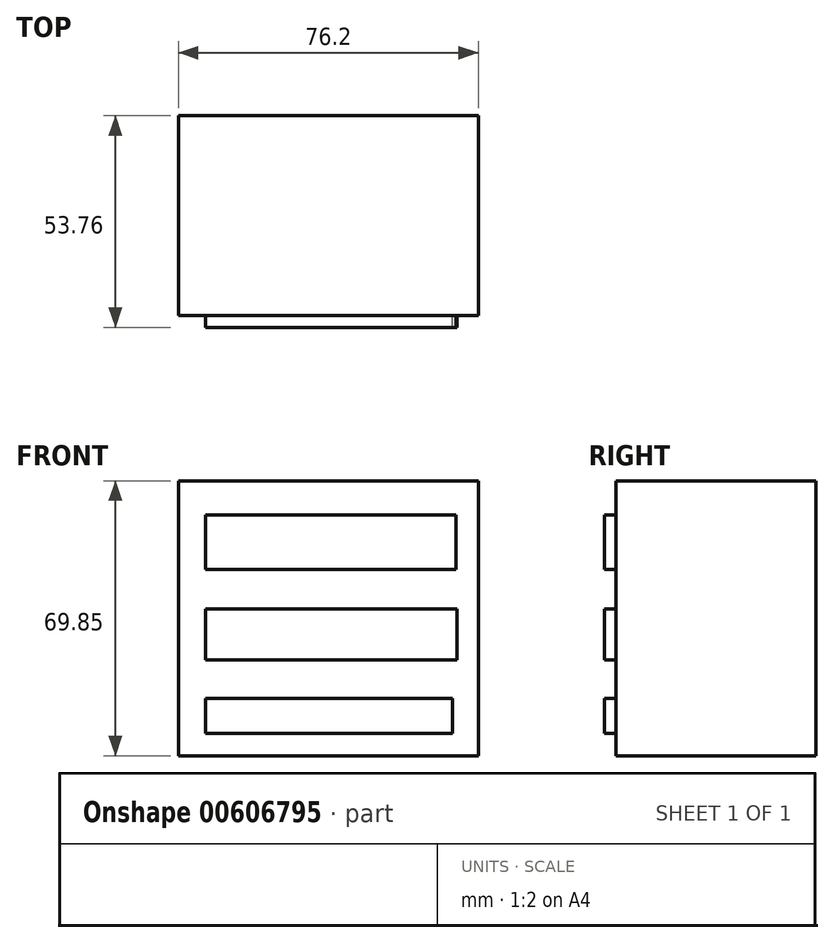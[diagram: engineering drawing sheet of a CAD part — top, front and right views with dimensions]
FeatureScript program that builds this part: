
annotation { "Feature Type Name" : "Feature", "Feature Type Description" : "" }
export const myFeature = defineFeature(function(context is Context, id is Id, definition is map)
    precondition{}
    {
        {
            var Q0;
            Q0=qCreatedBy(makeId("Top.planeOp"),FACE);
            var sketch = newSketch(context, id + "F0", { "sketchPlane" : qUnion([Q0])});
            skLineSegment(sketch, "E0.bottom", {"start": v(-35.26, 28.36) * mm, "end": v(40.94, 28.36) * mm});
            skLineSegment(sketch, "E0.top", {"start": v(-35.26, -22.44) * mm, "end": v(40.94, -22.44) * mm});
            skLineSegment(sketch, "E0.left", {"start": v(-35.26, 28.36) * mm, "end": v(-35.26, -22.44) * mm});
            skLineSegment(sketch, "E0.right", {"start": v(40.94, 28.36) * mm, "end": v(40.94, -22.44) * mm});
            skSolve(sketch);
        }
        {
            var Q0;
            Q0 = qSketchRegion(id + "F0", true);
            extrude(context, id + "F1", {"entities" : qUnion([Q0]), "depth" : 69.85 * mm, "offsetDistance" : 25.4 * mm});
        }
        {
            var Q0;
            Q0=qCreatedBy(makeId("Front.planeOp"),FACE);
            var sketch = newSketch(context, id + "F2", { "sketchPlane" : qUnion([Q0])});
            skLineSegment(sketch, "E1.bottom", {"start": v(-28.35, 61.17) * mm, "end": v(35.26, 61.17) * mm});
            skLineSegment(sketch, "E1.top", {"start": v(-28.35, 47.35) * mm, "end": v(35.26, 47.35) * mm});
            skLineSegment(sketch, "E1.left", {"start": v(-28.35, 61.17) * mm, "end": v(-28.35, 47.35) * mm});
            skLineSegment(sketch, "E1.right", {"start": v(35.26, 61.17) * mm, "end": v(35.26, 47.35) * mm});
            skLineSegment(sketch, "E2.bottom", {"start": v(-28.35, 37.28) * mm, "end": v(35.55, 37.28) * mm});
            skLineSegment(sketch, "E2.top", {"start": v(-28.35, 24.33) * mm, "end": v(35.55, 24.33) * mm});
            skLineSegment(sketch, "E2.left", {"start": v(-28.35, 37.28) * mm, "end": v(-28.35, 24.33) * mm});
            skLineSegment(sketch, "E2.right", {"start": v(35.55, 37.28) * mm, "end": v(35.55, 24.33) * mm});
            skLineSegment(sketch, "E3.bottom", {"start": v(-28.35, 14.54) * mm, "end": v(34.4, 14.54) * mm});
            skLineSegment(sketch, "E3.top", {"start": v(-28.35, 5.62) * mm, "end": v(34.4, 5.62) * mm});
            skLineSegment(sketch, "E3.left", {"start": v(-28.35, 14.54) * mm, "end": v(-28.35, 5.62) * mm});
            skLineSegment(sketch, "E3.right", {"start": v(34.4, 14.54) * mm, "end": v(34.4, 5.62) * mm});
            skSolve(sketch);
        }
        {
            var Q0;
            Q0 = qSketchRegion(id + "F2", true);
            extrude(context, id + "F3", {"entities" : qUnion([Q0]), "operationType" : NewBodyOperationType.ADD, "depth" : 25.4 * mm, "offsetDistance" : 25.4 * mm});
        }
    });
